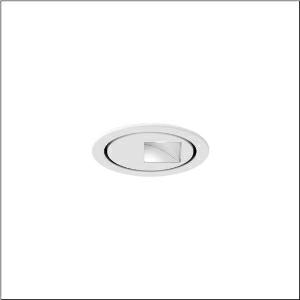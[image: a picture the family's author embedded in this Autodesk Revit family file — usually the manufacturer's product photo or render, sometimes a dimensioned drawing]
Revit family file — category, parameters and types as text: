
# Revit family: lunis_11_micro_round_51dj11b71wm21
name_source: partatom
category: Lighting Fixtures
units: mm (PartAtom-declared; Revit-internal decimal feet)

## family parameters
Cut with Voids When Loaded = No
Host = Face
Light Source = No
Part Type = Normal
Room Calculation Point = No
Round Connector Dimension = Use Diameter
Shared = No

## types (1)
- Lunis 11 micro round (1 x LED 3000K / CRI = 90 (unbekannt), 1100 lm, 3000K)
    Apparent Load = 20 VA
    CIE Flux Codes = 42 75 96 100 100
    Color Rendering = 90
    Color Temperature = 3000K
    Default Elevation = 1800 mm
    Description = Lunis 11 micro round, downlight, light control with wallwasher, of highly reflective aluminium, highly specular, light emission: direct distribution, LED rated luminous flux: 1.100lm, light colour: 930, with terminal, 3-pole, mains connection: 220..230V, AC, 50/60Hz, LED module, of aluminium, highly specular, white, diameter: 114mm, clamping range: 1..40mm, recessing ring, of plastic, traffic white (RAL 9016), protection rating (complete): IP20, insulation class (complete): insulation class II (safety insulation), certification: CE, permissible ambient temperature for indoor applications: 0..+35°C, packaging unit: 1 piece
    Height = 0 mm  [stored 0 ft]
    Lamp = 1 x LED 3000K / CRI >= 90 (unbekannt)
    Lamp Light Flux = 1100 lm
    Lamp count = 1
    Length = 114 mm
    Luminous efficacy = 56 lm/W
    Manufacturer = Siteco
    ModVariant = No
    Model = 51DJ11B71WM21
    Mounting Place = Ceiling
    Mounting Type = Recessed
    Number of Poles = 1
    OnlyDefault = Yes
    Power Factor = 1
    Product Name = Lunis 11 micro round
    Product group = downlight
    ProductGroupID = 400
    Protection Class = Protection class II
    Protection Degree = IP 20
    RLX_Detail_Level = 1
    RLX_Emergency_Light_Flux = 0 lm
    RLX_Emergency_Type = 0
    RLX_Emergency_Type_DB = No
    RlxData = <blob elided: 40601 chars, md5=1811518d>
    Socket = socket
    Standby Power = 0 W
    System Light Flux = 1100 lm
    System Power = 20 W
    Type Comments = Product without accessories
    Type Image = l_1004773.jpg
    URL = http://relux.com
    VarID = ---
    Voltage = 0 V
    Weight = 0.00 kg
    Width = 114 mm

note: [stored X ft] marks values corroborated as IEEE doubles in the binary element streams (Revit-internal decimal feet)

## geometry (parser evidence)
native form markers: Blend x4, Sweep x10
no freeform markers — native parametric forms only
